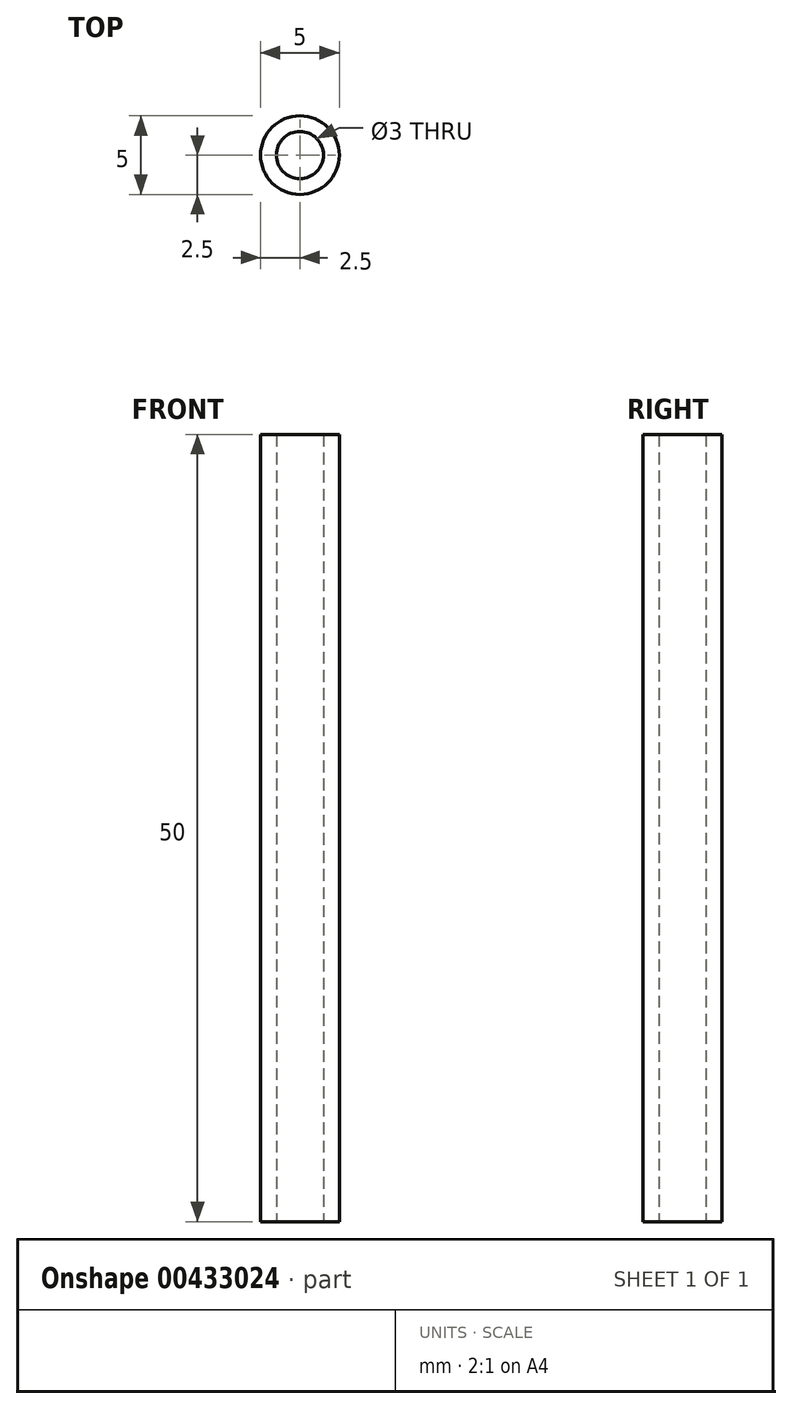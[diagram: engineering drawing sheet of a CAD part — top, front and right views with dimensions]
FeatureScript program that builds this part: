
annotation { "Feature Type Name" : "Feature", "Feature Type Description" : "" }
export const myFeature = defineFeature(function(context is Context, id is Id, definition is map)
    precondition{}
    {
        {
            var Q0;
            Q0=qCreatedBy(makeId("Top.planeOp"),FACE);
            var sketch = newSketch(context, id + "F0", { "sketchPlane" : qUnion([Q0])});
            skCircle(sketch, "E0", {"center": v(0, 0) * mm, "radius": 1.5 * mm});
            skCircle(sketch, "E1", {"center": v(0, 0) * mm, "radius": 2.5 * mm});
            skSolve(sketch);
        }
        {
            var Q0;
            Q0=makeQuery(id+"F0.imprint","IMPRINT",FACE,{"disambiguationData":[TD([[makeQuery(id+"F0.imprint","IMPRINT",EDGE,{"derivedFrom":sQuery(id+"F0.wireOp",EDGE,"E0")}),-1.0]])]});
            extrude(context, id + "F1", {"entities" : qUnion([Q0]), "offsetDistance" : 25 * mm, "depth" : 50 * mm});
        }
    });
